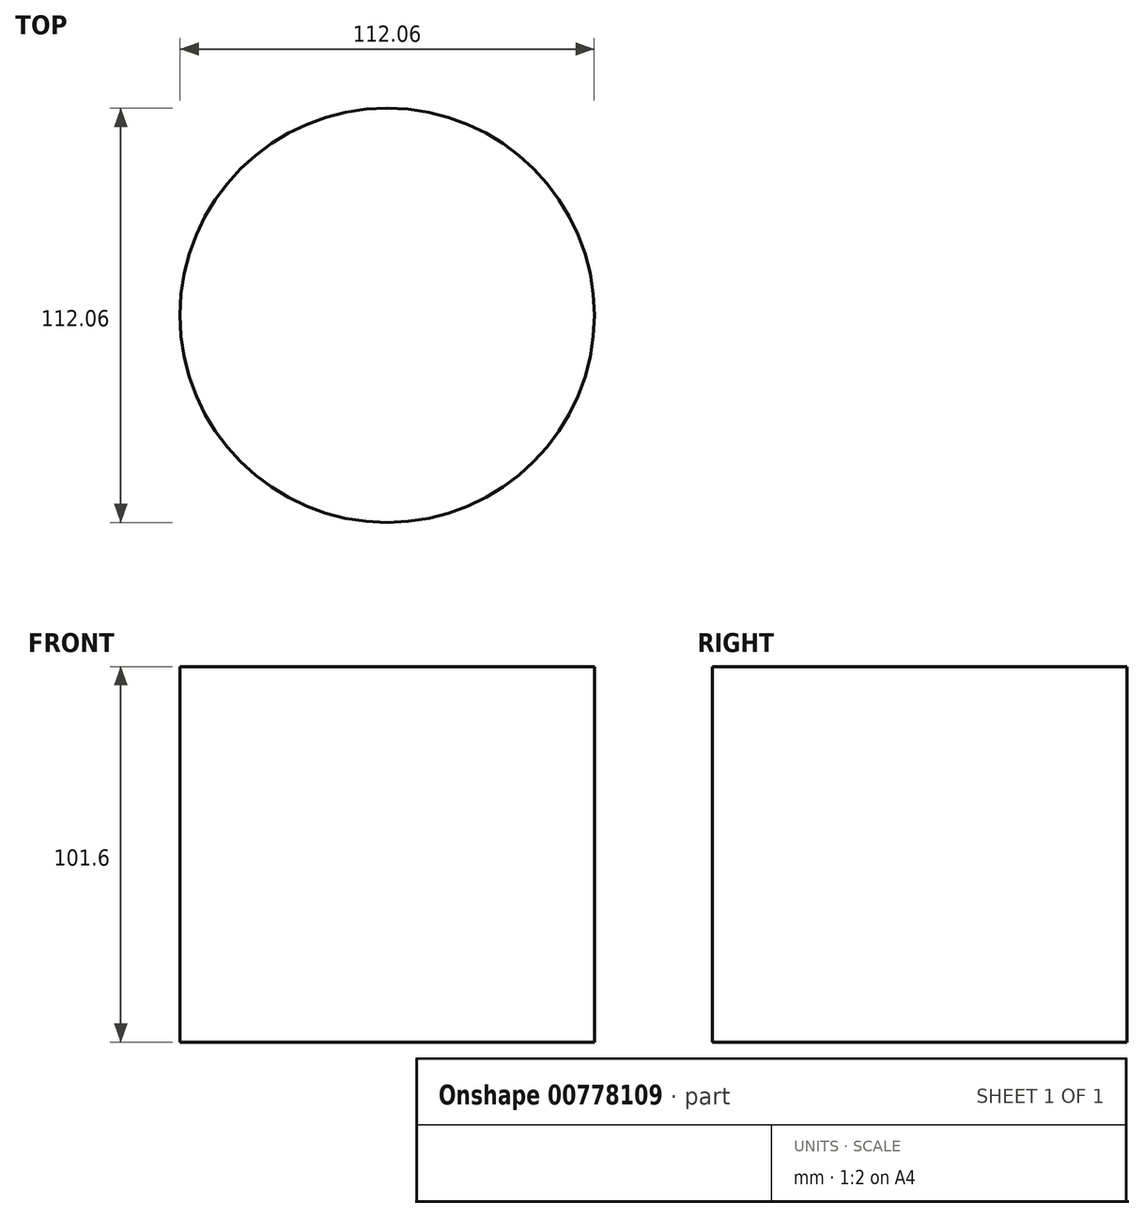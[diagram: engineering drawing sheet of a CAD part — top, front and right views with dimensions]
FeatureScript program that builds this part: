
annotation { "Feature Type Name" : "Feature", "Feature Type Description" : "" }
export const myFeature = defineFeature(function(context is Context, id is Id, definition is map)
    precondition{}
    {
        {
            var Q0;
            Q0=qCreatedBy(makeId("Top.planeOp"),FACE);
            var sketch = newSketch(context, id + "F0", { "sketchPlane" : qUnion([Q0])});
            skCircle(sketch, "E0", {"center": v(0, 0) * mm, "radius": 56.03 * mm});
            skSolve(sketch);
        }
        {
            var Q0;
            Q0=makeQuery(id+"F0.imprint","IMPRINT",FACE,{"disambiguationData":[TD([[makeQuery(id+"F0.imprint","IMPRINT",EDGE,{"derivedFrom":sQuery(id+"F0.wireOp",EDGE,"E0")}),1.0]])]});
            extrude(context, id + "F1", {"entities" : qUnion([Q0]), "depth" : 101.6 * mm, "offsetDistance" : 25.4 * mm});
        }
    });
